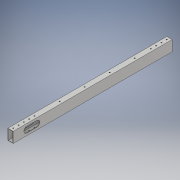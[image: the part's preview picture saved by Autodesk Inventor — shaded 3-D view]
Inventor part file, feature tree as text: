
AUTODESK INVENTOR PART (.ipt)
format: ipt  version: 2018 (Build 220112000, 112)  size: 189,440 bytes
history: native  units: in
note: dims shown in document units (in); Inventor stores cm internally (conversion verified against a paired STEP export)
features: extrude x6, sketch x6
ambient origin geometry x8: Origin, YZ Plane, XZ Plane, XY Plane, X Axis, Y Axis, Z Axis, Center Point
bodies: Solid1 (feature_tree)
feature tree (12):
  extrude  "Extrusion1"  Depth=2.0in
  sketch  "Sketch2"  dims[d2=0.0625in d3=30.0in d4=0.0in]
  extrude  "Extrusion4"  Depth=30.0in TaperAngle=0.0deg
  extrude  "Extrusion7"  Depth=4.724in
  extrude  "Extrusion8"  Depth=4.724in
  extrude  "Extrusion9"  Depth=0.5in
  extrude  "Extrusion11"  Depth=1.0in
  sketch  "Sketch1"  dims[d0=1.0in d1=2.0in]
  sketch  "Sketch3"  dims[d5=4.543in d6=4.724in]
  sketch  "Sketch6"  dims[d7=4.724in d8=4.724in]
  sketch  "Sketch7"  dims[d9=4.724in d10=0.5in]
  sketch  "Sketch8"  dims[d11=1.0in d12=1.0in d13=1.0in d14=0.2031in d15=0.2031in d16=0.2031in d18=0.2031in d19=0.2031in d20=0.2031in d21=0.2031in d27=0.5in d28=0.2031in d29=20.6875in d30=0.0in d53=3.5in d54=1.0in d55=2.0in d56=0.2031in d57=4.25in d58=0.0in d59=4.25in d60=0.0in d61=0.2031in d62=0.2031in d63=2.0in d64=3.0in d65=1.125in d66=1.0in d67=0.0in d68=1.5in d69=0.2031in d72=3.5in d73=2.0in d74=0.0in]
